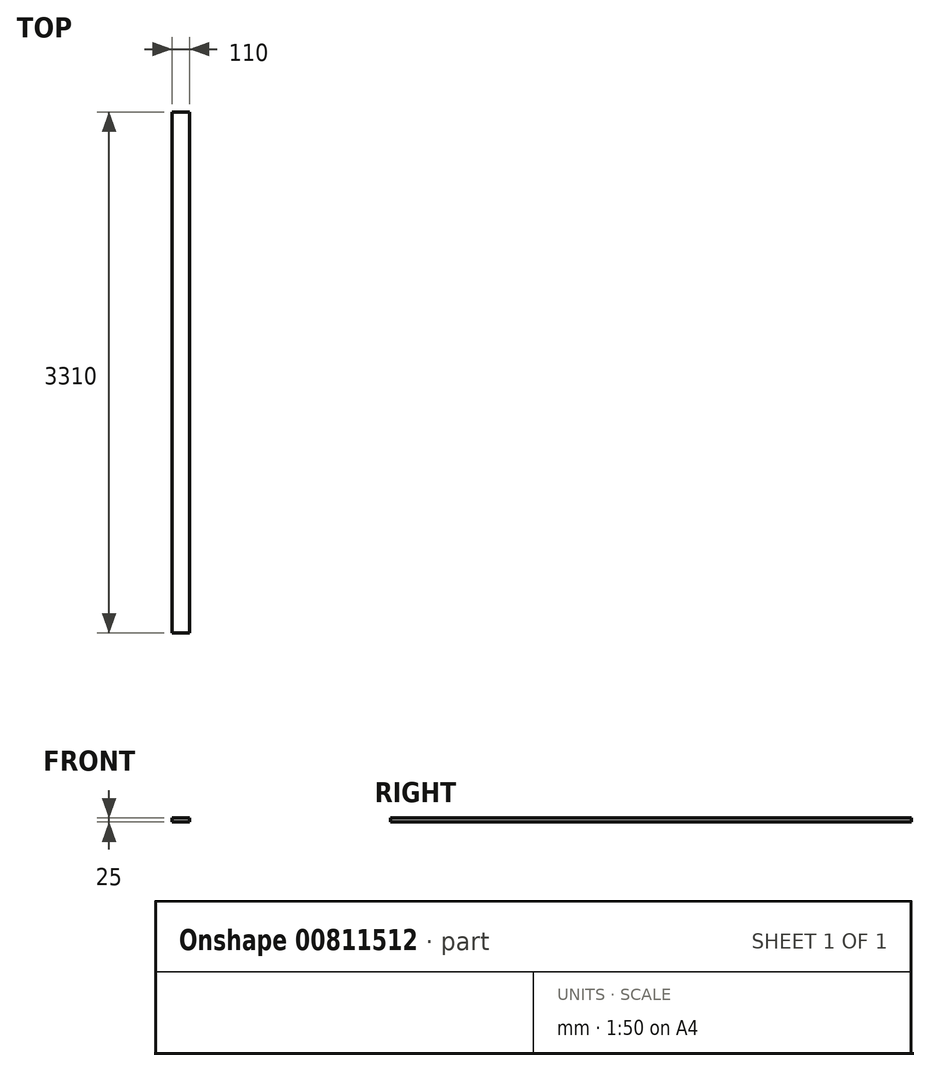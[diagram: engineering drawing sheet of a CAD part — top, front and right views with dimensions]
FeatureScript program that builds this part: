
annotation { "Feature Type Name" : "Feature", "Feature Type Description" : "" }
export const myFeature = defineFeature(function(context is Context, id is Id, definition is map)
    precondition{}
    {
        {
            var Q0;
            Q0=qCreatedBy(makeId("Top.planeOp"),FACE);
            var sketch = newSketch(context, id + "F0", { "sketchPlane" : qUnion([Q0])});
            skLineSegment(sketch, "E0.bottom", {"start": v(55, 1655) * mm, "end": v(-55, 1655) * mm});
            skLineSegment(sketch, "E0.top", {"start": v(55, -1655) * mm, "end": v(-55, -1655) * mm});
            skLineSegment(sketch, "E0.left", {"start": v(55, 1655) * mm, "end": v(55, -1655) * mm});
            skLineSegment(sketch, "E0.right", {"start": v(-55, 1655) * mm, "end": v(-55, -1655) * mm});
            skPoint(sketch, "E0.middle", {"position": v(0, 0) * mm});
            skSolve(sketch);
        }
        {
            var Q0;
            Q0=makeQuery(id+"F0.imprint","IMPRINT",FACE,{"disambiguationData":[TD([[makeQuery(id+"F0.imprint","IMPRINT",EDGE,{"derivedFrom":sQuery(id+"F0.wireOp",EDGE,"E0.bottom")}),1.0]])]});
            extrude(context, id + "F1", {"entities" : qUnion([Q0]), "depth" : 25 * mm, "offsetDistance" : 25 * mm});
        }
    });
